# Revit family: Aquarius Hand Towel Dispenser 6953 Family
name_source: partatom
category: Generic Models
revit_build: Autodesk Revit 2018 (Build: 20181011_1500(x64)
units: mm (PartAtom-declared; Revit-internal decimal feet)

## family parameters
Always vertical = Yes
Can host rebar = No
Cut with Voids When Loaded = No
Part Type = Normal
Room Calculation Point = No
Round Connector Dimension = Use Diameter
Shared = No
Work Plane-Based = No

## types (1)
- Aquarius Hand Towel Dispenser
    Depth = 191 mm  [stored 0.62664 ft]
    Height = 343 mm  [stored 1.12533 ft]
    Manufacturer = Kimberly Clark
    Material = Plastic
    Material 2 = Plastic panel
    Model = Aquarius Hand Towel Dispenser 6953
    Telephone = 011 456 5911
    URL = www.kcprofessional.co.za
    Width = 318 mm  [stored 1.04331 ft]

note: [stored X ft] marks values corroborated as IEEE doubles in the binary element streams (Revit-internal decimal feet)

## geometry (parser evidence)
native form markers: Sweep x1
no freeform markers — native parametric forms only
